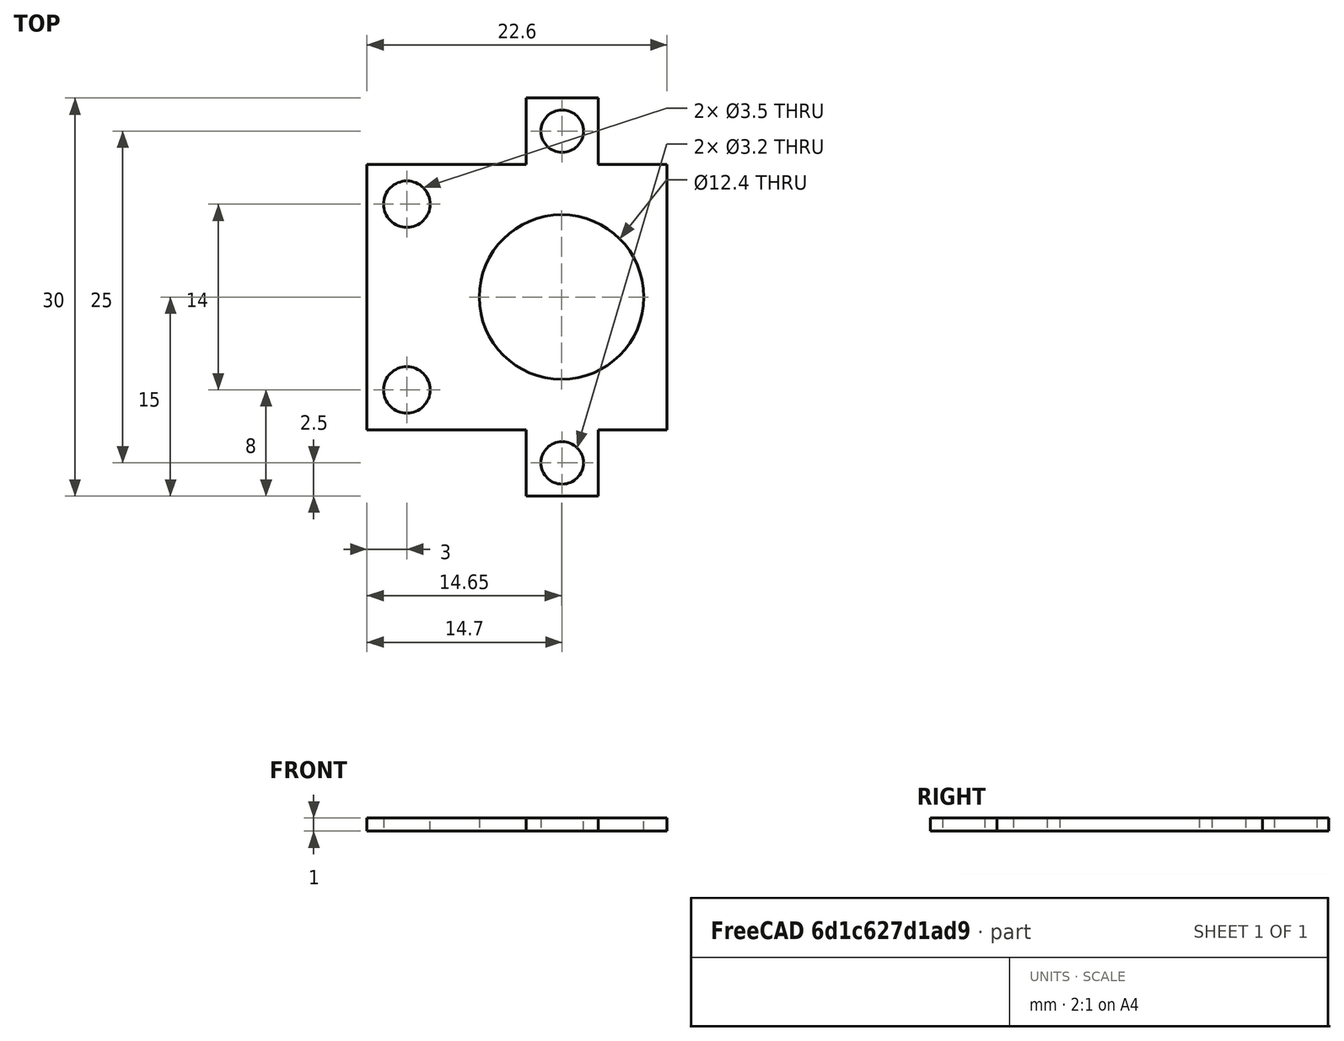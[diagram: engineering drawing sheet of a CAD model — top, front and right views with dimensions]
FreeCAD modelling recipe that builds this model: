
FCSTD DOCUMENT  (FreeCAD 0.17R13522 (Git))
Label: test_base_encoder_doble
License: CreativeCommons Attribution-ShareAlike
LicenseURL: http://creativecommons.org/licenses/by-sa/4.0/
objects: Part::Box×2, Part::Cut×2, Part::Feature×1
note: 5 computed .brp shape members not serialized (recipe doc carries the construction recipe); baked Part::Feature solids carry a one-line shape summary decoded from their .brp

FEATURE [Part::Feature] Pad001001  label="Pad021"
  shape: bbox 45.2 x 30 x 2 mm, 22 faces (baked)
FEATURE [Part::Box] Box  label="Cube"
  AttacherType = Attacher::AttachEngine3D
  Height = 10
  Length = 100
  Placement = pos=(-27,-24,1) rot=(0,0,1;0rad)
  Width = 100
FEATURE [Part::Cut] Cut
  Base = -> Pad001001
  Refine = true
  Tool = -> Box
FEATURE [Part::Box] Box001  label="Cube001"
  AttacherType = Attacher::AttachEngine3D
  Height = 10
  Length = 31
  Placement = pos=(0,-14,-5) rot=(0,0,1;0rad)
  Width = 29
FEATURE [Part::Cut] Cut001
  Base = -> Cut
  Refine = true
  Tool = -> Box001
